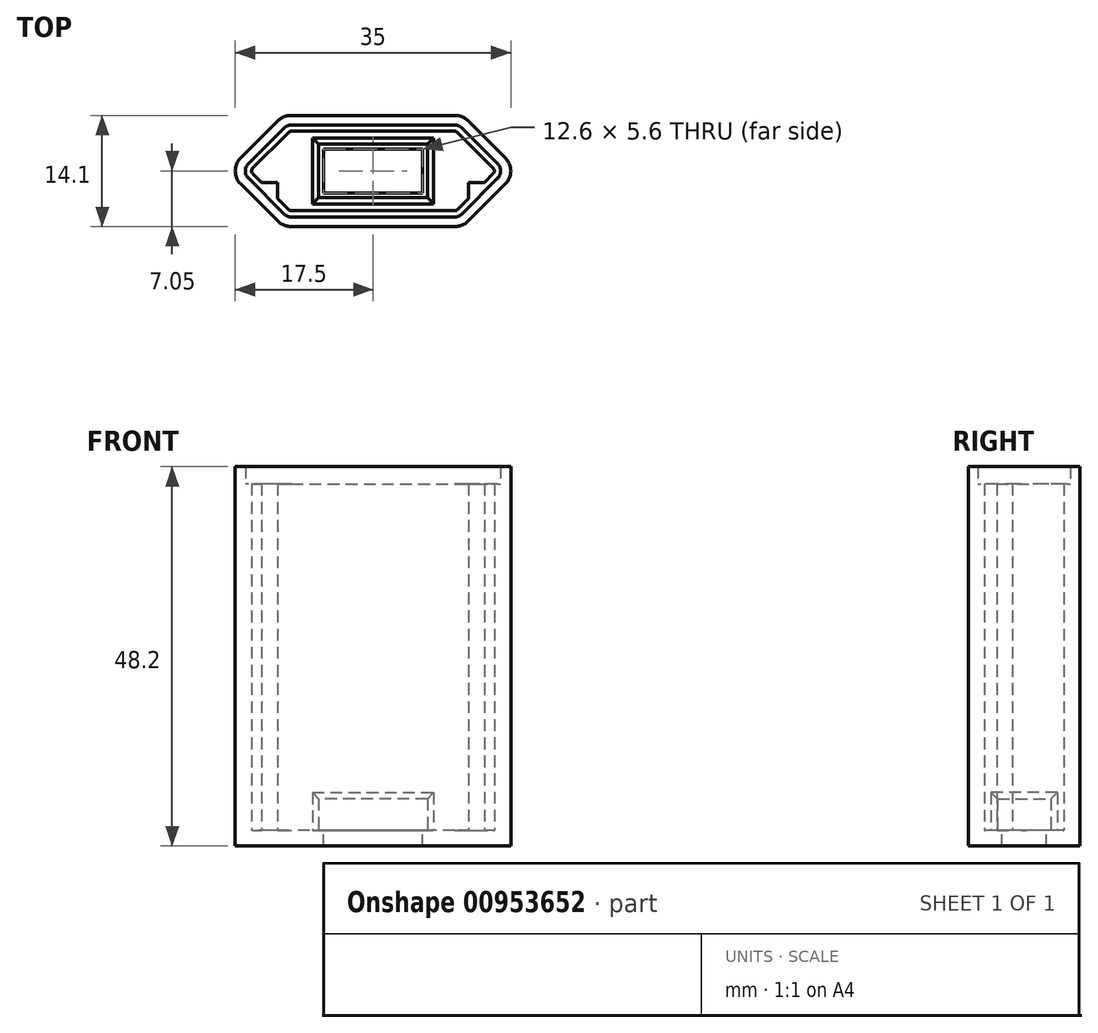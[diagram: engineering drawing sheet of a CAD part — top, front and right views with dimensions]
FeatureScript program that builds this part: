
annotation { "Feature Type Name" : "Feature", "Feature Type Description" : "" }
export const myFeature = defineFeature(function(context is Context, id is Id, definition is map)
    precondition{}
    {
        {
            var Q0;
            Q0=qCreatedBy(makeId("Top.planeOp"),FACE);
            var sketch = newSketch(context, id + "F0", { "sketchPlane" : qUnion([Q0])});
            skLineSegment(sketch, "E0", {"start": v(0, 7.05) * mm, "end": v(10.45, 7.05) * mm});
            skLineSegment(sketch, "E1", {"start": v(12.08, 6.38) * mm, "end": v(16.83, 1.63) * mm});
            skLineSegment(sketch, "E2", {"start": v(16.83, -1.63) * mm, "end": v(12.08, -6.38) * mm});
            skLineSegment(sketch, "E3", {"start": v(10.45, -7.05) * mm, "end": v(0, -7.05) * mm});
            skPoint(sketch, "E4.visualSharp", {"position": v(11.4, -7.05) * mm});
            skArc(sketch, "E4.filletArc", {"start": v(10.45, -7.05) * mm, "mid": v(11.33, -6.87) * mm, "end": v(12.08, -6.38) * mm});
            skPoint(sketch, "E5.visualSharp", {"position": v(18.45, 0) * mm});
            skArc(sketch, "E5.filletArc", {"start": v(16.83, -1.63) * mm, "mid": v(17.5, 0) * mm, "end": v(16.83, 1.63) * mm});
            skPoint(sketch, "E6.visualSharp", {"position": v(11.4, 7.05) * mm});
            skArc(sketch, "E6.filletArc", {"start": v(12.08, 6.38) * mm, "mid": v(11.33, 6.87) * mm, "end": v(10.45, 7.05) * mm});
            skLineSegment(sketch, "E7.0", {"start": v(10.37, -5.85) * mm, "end": v(0, -5.85) * mm});
            skLineSegment(sketch, "E7.1", {"start": v(15.84, -0.92) * mm, "end": v(11.29, -5.47) * mm});
            skLineSegment(sketch, "E7.2", {"start": v(11.29, 5.47) * mm, "end": v(15.84, 0.92) * mm});
            skLineSegment(sketch, "E7.3", {"start": v(0, 5.85) * mm, "end": v(10.37, 5.85) * mm});
            skLineSegment(sketch, "E8", {"start": v(0, 7.05) * mm, "end": v(0, 5.85) * mm});
            skLineSegment(sketch, "E9", {"start": v(0, -5.85) * mm, "end": v(0, -7.05) * mm});
            skPoint(sketch, "E10.visualSharp", {"position": v(16.76, 0) * mm});
            skArc(sketch, "E10.filletArc", {"start": v(15.84, -0.92) * mm, "mid": v(16.22, 0) * mm, "end": v(15.84, 0.92) * mm});
            skPoint(sketch, "E11.visualSharp", {"position": v(10.9, 5.85) * mm});
            skArc(sketch, "E11.filletArc", {"start": v(11.29, 5.47) * mm, "mid": v(10.86, 5.75) * mm, "end": v(10.37, 5.85) * mm});
            skPoint(sketch, "E12.visualSharp", {"position": v(10.9, -5.85) * mm});
            skArc(sketch, "E12.filletArc", {"start": v(10.37, -5.85) * mm, "mid": v(10.86, -5.75) * mm, "end": v(11.29, -5.47) * mm});
            skLineSegment(sketch, "E13", {"start": v(0, 5.85) * mm, "end": v(0, 2.8) * mm});
            skLineSegment(sketch, "E14", {"start": v(0, -5.85) * mm, "end": v(0, -2.8) * mm});
            skLineSegment(sketch, "E15", {"start": v(0, 2.8) * mm, "end": v(6.3, 2.8) * mm});
            skLineSegment(sketch, "E16", {"start": v(6.3, 2.8) * mm, "end": v(6.3, -2.8) * mm});
            skLineSegment(sketch, "E17", {"start": v(6.3, -2.8) * mm, "end": v(0, -2.8) * mm});
            skLineSegment(sketch, "E18", {"start": v(12.15, -3.47) * mm, "end": v(12.15, -1.47) * mm});
            skLineSegment(sketch, "E19", {"start": v(12.15, -1.47) * mm, "end": v(14.15, -1.47) * mm});
            skLineSegment(sketch, "E20.0", {"start": v(6.9, -3.4) * mm, "end": v(0, -3.4) * mm});
            skLineSegment(sketch, "E20.1", {"start": v(6.9, 3.4) * mm, "end": v(6.9, -3.4) * mm});
            skLineSegment(sketch, "E20.2", {"start": v(0, 3.4) * mm, "end": v(6.9, 3.4) * mm});
            skLineSegment(sketch, "E21.0", {"start": v(7.7, -4.2) * mm, "end": v(0, -4.2) * mm});
            skLineSegment(sketch, "E21.1", {"start": v(7.7, 4.2) * mm, "end": v(7.7, -4.2) * mm});
            skLineSegment(sketch, "E21.2", {"start": v(0, 4.2) * mm, "end": v(7.7, 4.2) * mm});
            skLineSegment(sketch, "E22.0", {"start": v(10.37, -5.05) * mm, "end": v(0, -5.05) * mm});
            skArc(sketch, "E22.1", {"start": v(10.37, -5.05) * mm, "mid": v(10.56, -5.01) * mm, "end": v(10.72, -4.9) * mm});
            skLineSegment(sketch, "E22.2", {"start": v(15.27, -0.35) * mm, "end": v(14.15, -1.47) * mm});
            skLineSegment(sketch, "E22.3", {"start": v(0, 5.05) * mm, "end": v(10.37, 5.05) * mm});
            skArc(sketch, "E22.4", {"start": v(10.72, 4.9) * mm, "mid": v(10.56, 5.01) * mm, "end": v(10.37, 5.05) * mm});
            skLineSegment(sketch, "E22.5", {"start": v(10.72, 4.9) * mm, "end": v(15.27, 0.35) * mm});
            skArc(sketch, "E22.6", {"start": v(15.27, -0.35) * mm, "mid": v(15.42, 0) * mm, "end": v(15.27, 0.35) * mm});
            skLineSegment(sketch, "E23.trimOffspring", {"start": v(12.15, -3.47) * mm, "end": v(10.72, -4.9) * mm});
            skSolve(sketch);
        }
        {
            var Q0;
            Q0=makeQuery(id+"F0.imprint","IMPRINT",FACE,{"disambiguationData":[TD([[makeQuery(id+"F0.imprint","IMPRINT",EDGE,{"derivedFrom":sQuery(id+"F0.wireOp",EDGE,"E18")}),1.0]])]});
            var Q1;
            {var subQ3=sQuery(id+"F0.wireOp",EDGE,"E15");Q1=makeQuery(id+"F0.imprint","IMPRINT",FACE,{"disambiguationData":[TD([[makeQuery(id+"F0.imprint","IMPRINT",EDGE,{"derivedFrom":subQ3}),1.0]])]});}
            var Q2;
            {var subQ0=sQuery(id+"F0.wireOp",EDGE,"E20.0");Q2=makeQuery(id+"F0.imprint","IMPRINT",FACE,{"disambiguationData":[TD([[makeQuery(id+"F0.imprint","IMPRINT",EDGE,{"derivedFrom":subQ0}),1.0]])]});}
            var Q3;
            Q3=makeQuery(id+"F0.imprint","IMPRINT",FACE,{"disambiguationData":[TD([[makeQuery(id+"F0.imprint","IMPRINT",EDGE,{"derivedFrom":sQuery(id+"F0.wireOp",EDGE,"E0")}),-1.0]])]});
            var Q4;
            {var subQ3=sQuery(id+"F0.wireOp",EDGE,"E7.0");Q4=makeQuery(id+"F0.imprint","IMPRINT",FACE,{"disambiguationData":[TD([[makeQuery(id+"F0.imprint","IMPRINT",EDGE,{"derivedFrom":subQ3}),-1.0]])]});}
            extrude(context, id + "F1", {"entities" : qUnion([Q0, Q1, Q2, Q3, Q4]), "oppositeDirection" : true, "depth" : 2 * mm, "offsetDistance" : 25 * mm});
        }
        {
            var Q0;
            {var subQ3=sQuery(id+"F0.wireOp",EDGE,"E20.0");Q0=makeQuery(id+"F0.imprint","IMPRINT",FACE,{"disambiguationData":[TD([[makeQuery(id+"F0.imprint","IMPRINT",EDGE,{"derivedFrom":subQ3}),1.0]])]});}
            extrude(context, id + "F2", {"entities" : qUnion([Q0]), "operationType" : NewBodyOperationType.ADD, "depth" : 5 * mm, "offsetDistance" : 25 * mm});
        }
        {
            var Q0;
            {var subQ0=sQuery(id+"F0.wireOp",EDGE,"oT0QAoJG-2ySH-ql9N-4A53-yntYT6HwSlEy");Q0=makeQuery(id+"F0.imprint","IMPRINT",FACE,{"disambiguationData":[TD([[makeQuery(id+"F0.imprint","IMPRINT",EDGE,{"derivedFrom":subQ0}),1.0]])]});}
            var Q1;
            {var subQ0=sQuery(id+"F0.wireOp",EDGE,"E18");Q1=makeQuery(id+"F0.imprint","IMPRINT",FACE,{"disambiguationData":[TD([[makeQuery(id+"F0.imprint","IMPRINT",EDGE,{"derivedFrom":subQ0}),-1.0]])]});}
            extrude(context, id + "F3", {"entities" : qUnion([Q0, Q1]), "operationType" : NewBodyOperationType.ADD, "depth" : 44 * mm, "offsetDistance" : 25 * mm});
        }
        {
            var Q0;
            Q0=makeQuery(id+"F0.imprint","IMPRINT",FACE,{"disambiguationData":[TD([[makeQuery(id+"F0.imprint","IMPRINT",EDGE,{"derivedFrom":sQuery(id+"F0.wireOp",EDGE,"E0")}),-1.0]])]});
            extrude(context, id + "F4", {"entities" : qUnion([Q0]), "operationType" : NewBodyOperationType.ADD, "depth" : 46.2 * mm, "offsetDistance" : 25 * mm});
        }
        {
            var Q0;
            Q0=makeQuery(id+"F1.opExtrude","SWEPT_BODY",BODY,{"disambiguationData":[OSD([sQuery(id+"F0.wireOp",EDGE,"E0"),sQuery(id+"F0.wireOp",EDGE,"E1"),sQuery(id+"F0.wireOp",EDGE,"E2"),sQuery(id+"F0.wireOp",EDGE,"E3"),sQuery(id+"F0.wireOp",EDGE,"E4.filletArc"),sQuery(id+"F0.wireOp",EDGE,"E5.filletArc"),sQuery(id+"F0.wireOp",EDGE,"E6.filletArc"),sQuery(id+"F0.wireOp",EDGE,"E8"),sQuery(id+"F0.wireOp",EDGE,"E9"),sQuery(id+"F0.wireOp",EDGE,"E13"),sQuery(id+"F0.wireOp",EDGE,"E14"),sQuery(id+"F0.wireOp",EDGE,"E15"),sQuery(id+"F0.wireOp",EDGE,"E16"),sQuery(id+"F0.wireOp",EDGE,"E17")])]});
            var Q1;
            {var subQ0=sQuery(id+"F0.wireOp",EDGE,"E8");var subQ1=sQuery(id+"F0.wireOp",EDGE,"E13");Q1=makeQuery(id+"F4.boolean.opBoolean","MERGE",FACE,{"derivedFrom":[makeQuery(id+"F2.boolean.opBoolean","MERGE",FACE,{"derivedFrom":[makeQuery(id+"F1.opExtrude","SWEPT_FACE",FACE,{"disambiguationData":[OSD([subQ0,subQ1])]}),makeQuery(id+"F2.opExtrude","SWEPT_FACE",FACE,{"disambiguationData":[OSD([subQ1])]})]}),makeQuery(id+"F4.opExtrude","SWEPT_FACE",FACE,{"disambiguationData":[OSD([subQ0])]})]});}
            mirror(context, id + "F5", {"operationType" : NewBodyOperationType.ADD, "entities" : qUnion([Q0]), "mirrorPlane" : qUnion([Q1])});
        }
        {
            var Q0;
            Q0=makeQuery(id+"F2.opExtrude","CAP_EDGE",EDGE,{"disambiguationData":[OSD([sQuery(id+"F0.wireOp",EDGE,"E20.1")])],"isStart":false});
            var Q1;
            {var subQ0=makeQuery(id+"F2.opExtrude","CAP_EDGE",EDGE,{"disambiguationData":[OSD([sQuery(id+"F0.wireOp",EDGE,"E20.2")])],"isStart":false});Q1=makeQuery(id+"F5.boolean.opBoolean","MERGE",EDGE,{"derivedFrom":[subQ0,makeQuery(id+"F5.opPattern","COPY",EDGE,{"derivedFrom":subQ0,"instanceName":"1"})]});}
            var Q2;
            {var subQ0=makeQuery(id+"F2.opExtrude","CAP_EDGE",EDGE,{"disambiguationData":[OSD([sQuery(id+"F0.wireOp",EDGE,"E20.0")])],"isStart":false});Q2=makeQuery(id+"F5.boolean.opBoolean","MERGE",EDGE,{"derivedFrom":[subQ0,makeQuery(id+"F5.opPattern","COPY",EDGE,{"derivedFrom":subQ0,"instanceName":"1"})]});}
            var Q3;
            Q3=makeQuery(id+"F5.opPattern","COPY",EDGE,{"derivedFrom":makeQuery(id+"F2.opExtrude","CAP_EDGE",EDGE,{"disambiguationData":[OSD([sQuery(id+"F0.wireOp",EDGE,"E20.1")])],"isStart":false}),"instanceName":"1"});
            chamfer(context, id + "F6", {"entities" : qUnion([Q0, Q1, Q2, Q3]), "width" : 1 * mm, "tangentPropagation" : true});
        }
    });
